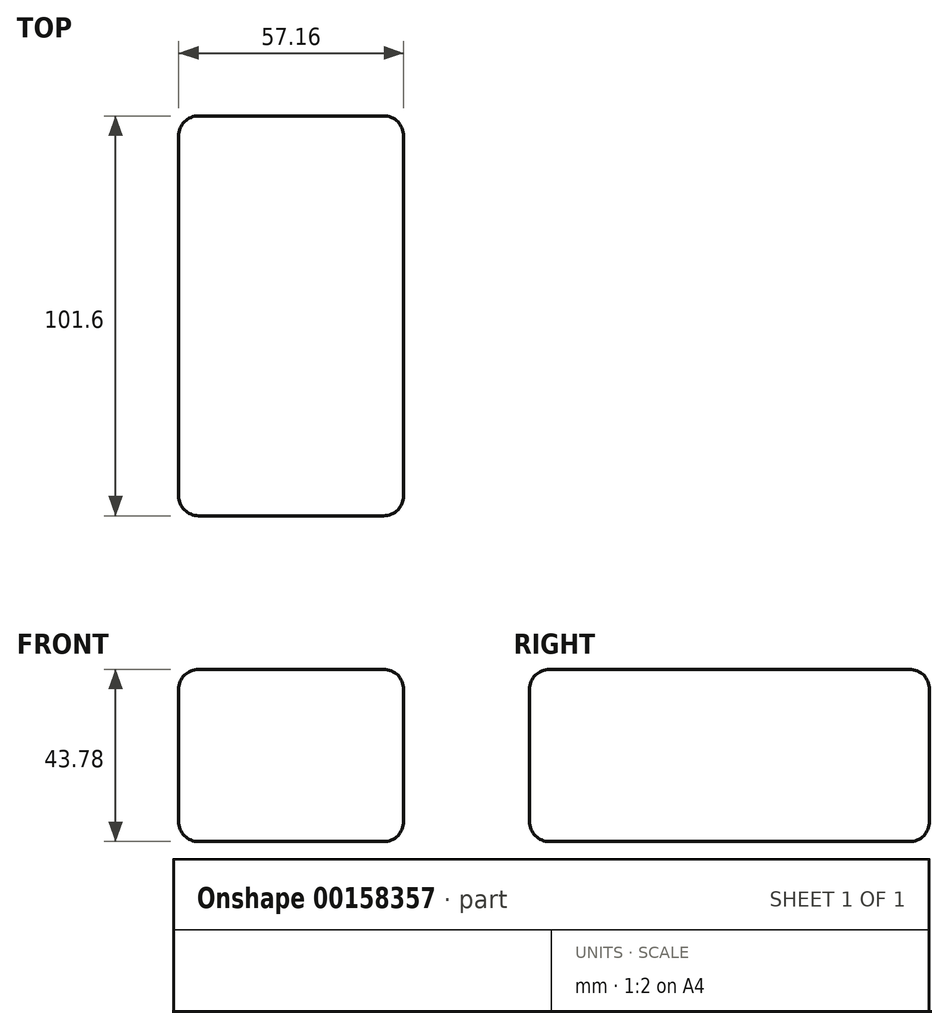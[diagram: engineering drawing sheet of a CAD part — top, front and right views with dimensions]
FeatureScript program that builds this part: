
annotation { "Feature Type Name" : "Feature", "Feature Type Description" : "" }
export const myFeature = defineFeature(function(context is Context, id is Id, definition is map)
    precondition{}
    {
        {
            var Q0;
            Q0=qCreatedBy(makeId("Front.planeOp"),FACE);
            var sketch = newSketch(context, id + "F0", { "sketchPlane" : qUnion([Q0])});
            skLineSegment(sketch, "E0.bottom", {"start": v(0, 0) * mm, "end": v(57.16, 0) * mm});
            skLineSegment(sketch, "E0.top", {"start": v(0, 43.78) * mm, "end": v(57.16, 43.78) * mm});
            skLineSegment(sketch, "E0.left", {"start": v(0, 0) * mm, "end": v(0, 43.78) * mm});
            skLineSegment(sketch, "E0.right", {"start": v(57.16, 0) * mm, "end": v(57.16, 43.78) * mm});
            skSolve(sketch);
        }
        {
            var Q0;
            Q0=makeQuery(id+"F0.imprint","IMPRINT",FACE,{"disambiguationData":[TD([[makeQuery(id+"F0.imprint","IMPRINT",EDGE,{"derivedFrom":sQuery(id+"F0.wireOp",EDGE,"E0.bottom")}),1.0]])]});
            extrude(context, id + "F1", {"entities" : qUnion([Q0]), "depth" : 101.6 * mm});
        }
        {
            var Q0;
            Q0=makeQuery(id+"F1.opExtrude","CAP_EDGE",EDGE,{"disambiguationData":[OSD([sQuery(id+"F0.wireOp",EDGE,"E0.top")])],"isStart":false});
            var Q1;
            Q1=makeQuery(id+"F1.opExtrude","CAP_EDGE",EDGE,{"disambiguationData":[OSD([sQuery(id+"F0.wireOp",EDGE,"E0.right")])],"isStart":false});
            var Q2;
            Q2=makeQuery(id+"F1.opExtrude","SWEPT_EDGE",EDGE,{"disambiguationData":[OSD([sQuery(id+"F0.wireOp",EDGE,"E0.top"),sQuery(id+"F0.wireOp",EDGE,"E0.right")])]});
            var Q3;
            Q3=makeQuery(id+"F1.opExtrude","SWEPT_EDGE",EDGE,{"disambiguationData":[OSD([sQuery(id+"F0.wireOp",EDGE,"E0.top"),sQuery(id+"F0.wireOp",EDGE,"E0.left")])]});
            var Q4;
            Q4=makeQuery(id+"F1.opExtrude","CAP_EDGE",EDGE,{"disambiguationData":[OSD([sQuery(id+"F0.wireOp",EDGE,"E0.left")])],"isStart":false});
            var Q5;
            Q5=makeQuery(id+"F1.opExtrude","CAP_EDGE",EDGE,{"disambiguationData":[OSD([sQuery(id+"F0.wireOp",EDGE,"E0.right")])],"isStart":true});
            var Q6;
            Q6=makeQuery(id+"F1.opExtrude","SWEPT_FACE",FACE,{"disambiguationData":[OSD([sQuery(id+"F0.wireOp",EDGE,"E0.top")])]});
            var Q7;
            Q7=makeQuery(id+"F1.opExtrude","SWEPT_EDGE",EDGE,{"disambiguationData":[OSD([sQuery(id+"F0.wireOp",EDGE,"E0.bottom"),sQuery(id+"F0.wireOp",EDGE,"E0.right")])]});
            var Q8;
            Q8=makeQuery(id+"F1.opExtrude","SWEPT_FACE",FACE,{"disambiguationData":[OSD([sQuery(id+"F0.wireOp",EDGE,"E0.bottom")])]});
            var Q9;
            Q9=makeQuery(id+"F1.opExtrude","CAP_EDGE",EDGE,{"disambiguationData":[OSD([sQuery(id+"F0.wireOp",EDGE,"E0.left")])],"isStart":true});
            fillet(context, id + "F2", {"entities" : qUnion([Q0, Q1, Q2, Q3, Q4, Q5, Q6, Q7, Q8, Q9]), "radius" : 5.08 * mm, "tangentPropagation" : true, "allowEdgeOverflow" : false});
        }
    });
